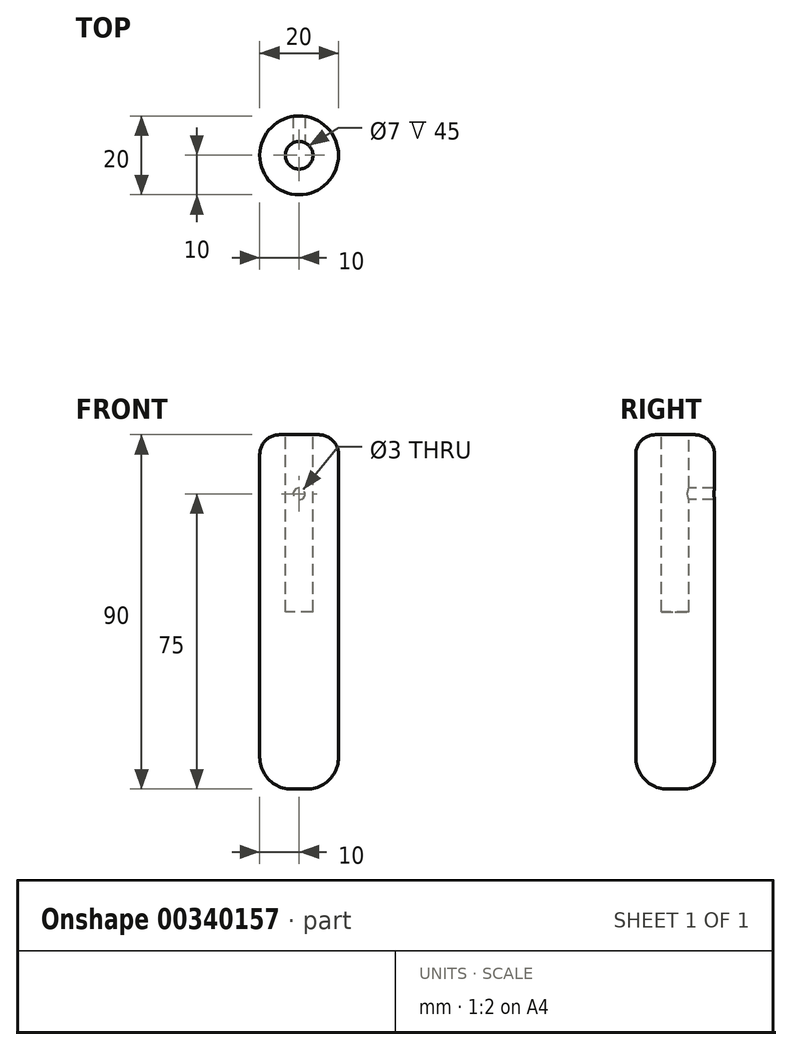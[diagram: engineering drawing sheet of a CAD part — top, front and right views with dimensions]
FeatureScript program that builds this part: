
annotation { "Feature Type Name" : "Feature", "Feature Type Description" : "" }
export const myFeature = defineFeature(function(context is Context, id is Id, definition is map)
    precondition{}
    {
        {
            var Q0;
            Q0=qCreatedBy(makeId("Top.planeOp"),FACE);
            var sketch = newSketch(context, id + "F0", { "sketchPlane" : qUnion([Q0])});
            skCircle(sketch, "E0", {"center": v(0, 0) * mm, "radius": 10 * mm});
            skSolve(sketch);
        }
        {
            var Q0;
            Q0 = qSketchRegion(id + "F0", true);
            extrude(context, id + "F1", {"entities" : qUnion([Q0]), "depth" : 90 * mm});
        }
        {
            var Q0;
            Q0=makeQuery(id+"F1.opExtrude","CAP_EDGE",EDGE,{"disambiguationData":[OSD([sQuery(id+"F0.wireOp",EDGE,"E0")])],"isStart":true});
            fillet(context, id + "F2", {"entities" : qUnion([Q0]), "radius" : 8 * mm, "tangentPropagation" : true, "allowEdgeOverflow" : false});
        }
        {
            var Q0;
            Q0=makeQuery(id+"F1.opExtrude","CAP_EDGE",EDGE,{"disambiguationData":[OSD([sQuery(id+"F0.wireOp",EDGE,"E0")])],"isStart":false});
            fillet(context, id + "F3", {"entities" : qUnion([Q0]), "radius" : 5 * mm, "tangentPropagation" : true, "allowEdgeOverflow" : false});
        }
        {
            var Q0;
            Q0=makeQuery(id+"F1.opExtrude","CAP_FACE",FACE,{"disambiguationData":[OSD([sQuery(id+"F0.wireOp",EDGE,"E0")])],"isStart":false});
            var sketch = newSketch(context, id + "F4", { "sketchPlane" : qUnion([Q0])});
            skCircle(sketch, "E1", {"center": v(0, 0) * mm, "radius": 3.5 * mm});
            skSolve(sketch);
        }
        {
            var Q0;
            Q0=makeQuery(id+"F4.imprint","IMPRINT",FACE,{"disambiguationData":[TD([[makeQuery(id+"F4.imprint","IMPRINT",EDGE,{"derivedFrom":sQuery(id+"F4.wireOp",EDGE,"E1")}),1.0]])]});
            extrude(context, id + "F5", {"entities" : qUnion([Q0]), "operationType" : NewBodyOperationType.REMOVE, "oppositeDirection" : true, "depth" : 45 * mm});
        }
        {
            var Q0;
            Q0=qCreatedBy(makeId("Front.planeOp"),FACE);
            var sketch = newSketch(context, id + "F6", { "sketchPlane" : qUnion([Q0])});
            skLineSegment(sketch, "E2.0", {"start": v(-3.5, 90) * mm, "end": v(3.5, 90) * mm});
            skPoint(sketch, "E3", {"position": v(0, 90) * mm});
            skCircle(sketch, "E4", {"center": v(0, 75) * mm, "radius": 1.5 * mm});
            skSolve(sketch);
        }
        {
            var Q0;
            Q0 = qSketchRegion(id + "F6", true);
            extrude(context, id + "F7", {"entities" : qUnion([Q0]), "operationType" : NewBodyOperationType.REMOVE, "endBound" : BoundingType.THROUGH_ALL, "oppositeDirection" : true, "depth" : -24.9 * mm});
        }
    });
